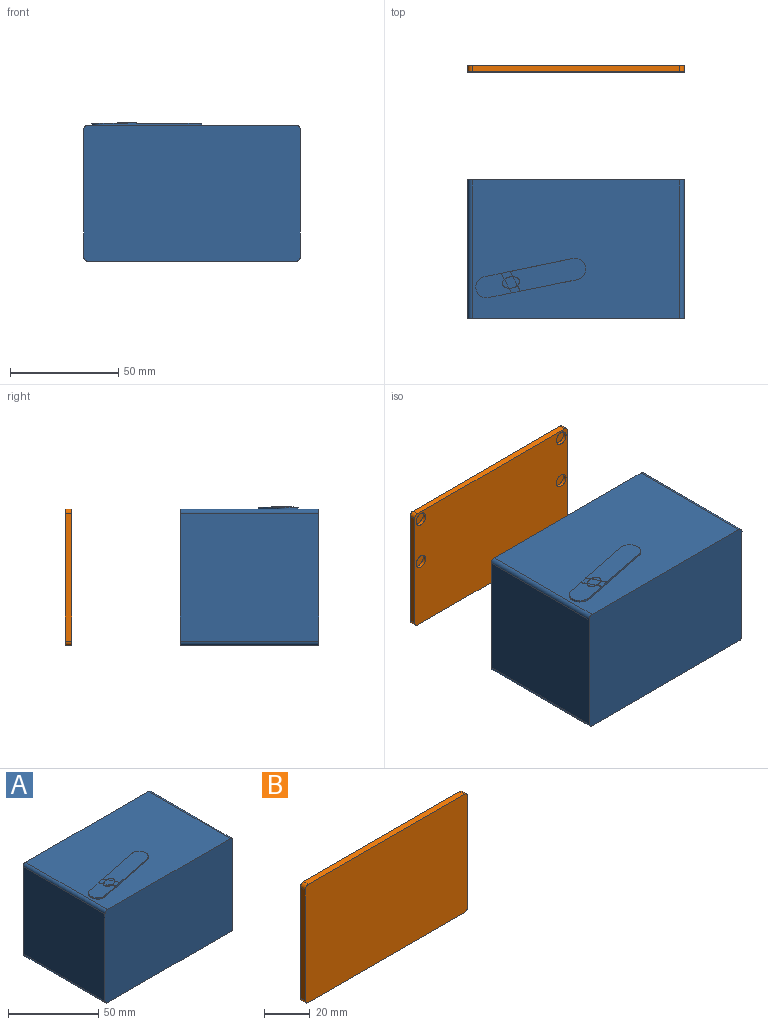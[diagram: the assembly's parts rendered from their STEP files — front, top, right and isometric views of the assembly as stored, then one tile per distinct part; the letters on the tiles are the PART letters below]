
ASSEMBLY  parts=2 mates=1
PART A: 54 faces, bbox 100x64x64.2 mm
  f0: plane 5.34x3.69mm, normal (0,0,1), area 10.9mm2, adj f42,f47,f48,f51
  f1: plane 96x64mm, normal (0,0,1), area 5652.7mm2, adj f2,f7,f39,f40,f41,f42,f43,f45
  f2: plane 100x63mm, normal (0,1,0), area 2484.3mm2, adj f1,f3,f4,f6,f8,f9,f10,f11
  f3: plane 48.15x29.5mm, normal (0,0,-1), area 1420.4mm2, adj f2,f5,f14,f18
  f4: plane 48.15x29.5mm, normal (0,0,1), area 1420.4mm2, adj f2,f5,f14,f18
  f5: cylinder r=14.35mm len=29.5mm, axis (1,0,0), area 1329.9mm2, adj f3,f4,f14,f18
  f6: plane 64x59mm, normal (-1,0,0), area 3776mm2, adj f2,f7,f37,f39
  f7: plane 100x63mm, normal (0,-1,0), area 6296.6mm2, adj f1,f6,f8,f9,f37,f38,f39,f40
  f8: plane 64x59mm, normal (1,0,0), area 3776mm2, adj f2,f7,f38,f40
  f9: plane 96x64mm, normal (0,0,-1), area 6144mm2, adj f2,f7,f37,f38
  f10: plane 62.5x28.7mm, normal (1,0,0), area 1705.4mm2, adj f2,f11,f12,f13
  f11: plane 59.5x48.15mm, normal (0,0,-1), area 2864.9mm2, adj f2,f10,f13,f16
  f12: plane 59.5x48.15mm, normal (0,0,1), area 2864.9mm2, adj f2,f10,f13,f16
  f13: cylinder r=14.35mm len=59.5mm, axis (1,0,0), area 2682.4mm2, adj f10,f11,f12,f16
  f14: plane 62.5x28.7mm, normal (-1,0,0), area 1705.4mm2, adj f2,f3,f4,f5
  f15: plane 63x7.5mm, normal (0,0,-1), area 472.5mm2, adj f2,f16,f18,f19
  f16: plane 63x30.7mm, normal (1,0,0), area 228.7mm2, adj f2,f11,f12,f13,f15,f17,f19
  f17: plane 63x7.5mm, normal (0,0,1), area 472.5mm2, adj f2,f16,f18,f19
  f18: plane 63x30.7mm, normal (-1,0,0), area 228.7mm2, adj f2,f3,f4,f5,f15,f17,f19
  f19: plane 30.7x7.5mm, normal (0,1,0), area 230.2mm2, adj f15,f16,f17,f18
  f20: plane 73x42mm, normal (0,0,1), area 2851mm2, adj f2,f21,f23,f24,f25,f27,f28
  f21: plane 42x12mm, normal (1,0,0), area 504mm2, adj f2,f20,f22,f24
  f22: plane 73x42mm, normal (0,0,-1), area 3066mm2, adj f2,f21,f23,f24
  f23: plane 42x12mm, normal (-1,0,0), area 504mm2, adj f2,f20,f22,f24
  f24: plane 73x12mm, normal (0,1,0), area 876mm2, adj f20,f21,f22,f23
  f25: plane 25x3mm, normal (-1,0,0), area 75mm2, adj f2,f20,f26,f28
  f26: plane 25x8.6mm, normal (0,0,1), area 215mm2, adj f2,f25,f27,f28
  f27: plane 25x3mm, normal (1,0,0), area 75mm2, adj f2,f20,f26,f28
  f28: plane 8.6x3mm, normal (0,1,0), area 25.8mm2, adj f20,f25,f26,f27
  f29: cylinder r=3.17mm len=6.33mm, axis (0,1,0), area 32mm2, adj f2,f30
  f30: plane 6.33x6.33mm, normal (0,1,0), area 31.5mm2, adj f29
  f31: cylinder r=3.17mm len=6.33mm, axis (0,1,0), area 32mm2, adj f2,f32
  f32: plane 6.33x6.33mm, normal (0,1,0), area 31.5mm2, adj f31
  f33: cylinder r=3.17mm len=6.33mm, axis (0,1,0), area 32mm2, adj f2,f34
  f34: plane 6.33x6.33mm, normal (0,1,0), area 31.5mm2, adj f33
  f35: cylinder r=3.17mm len=6.33mm, axis (0,1,0), area 32mm2, adj f2,f36
  f36: plane 6.33x6.33mm, normal (0,1,0), area 31.5mm2, adj f35
  f37: cylinder r=2mm len=64mm, axis (0,-1,0), area 201.1mm2, adj f2,f6,f7,f9
  f38: cylinder r=2mm len=64mm, axis (0,1,0), area 201.1mm2, adj f2,f7,f8,f9
  f39: cylinder r=2mm len=64mm, axis (0,1,0), area 201.1mm2, adj f1,f2,f6,f7
  f40: cylinder r=2mm len=64mm, axis (0,-1,0), area 201.1mm2, adj f1,f2,f7,f8
  f41: plane 39.89x8.05mm, normal (0.2,-0.98,0), area 33.4mm2, adj f1,f43,f44,f45,f46,f47,f48,f49
  f42: plane 39.83x8.24mm, normal (-0.2,0.98,0), area 33.4mm2, adj f0,f1,f43,f44,f45,f46,f47,f48
  f43: cylinder r=5mm len=10mm, axis (0,0,-1), area 14.2mm2, adj f1,f41,f42,f44
  f44: plane 16.54x11.41mm, normal (0,0,1), area 131.4mm2, adj f41,f42,f43,f47
  f45: cylinder r=5mm len=9.9mm, axis (0,0,-1), area 12.6mm2, adj f1,f41,f42,f46
  f46: plane 34.96x15.19mm, normal (0,0,1), area 318.9mm2, adj f41,f42,f45,f48
  f47: plane 9.08x4.73mm, normal (-0.89,-0.46,0), area 2mm2, adj f0,f41,f42,f44,f49,f50
  f48: plane 9.1x4.74mm, normal (0.89,0.46,0), area 2.1mm2, adj f0,f41,f42,f46,f49,f53
  f49: plane 5.2x3.45mm, normal (0,0,1), area 9.8mm2, adj f41,f47,f48,f51
  f50: plane 4.08x3.1mm, normal (0,0,-1), area 6.2mm2, adj f47,f51
  f51: extruded ~7.85x5.33mm, area 4.2mm2, adj f0,f49,f50,f52,f53
  f52: plane 7.86x5.35mm, normal (0,0,1), area 32.6mm2, adj f51
  f53: plane 4.04x3.04mm, normal (0,0,-1), area 6mm2, adj f48,f51
PART B: 18 faces, bbox 100x3x63 mm
  f0: plane 59x3mm, normal (1,0,0), area 177mm2, adj f4,f5,f14,f17
  f1: plane 96x3mm, normal (0,0,1), area 288mm2, adj f4,f5,f14,f15
  f2: plane 59x3mm, normal (-1,0,0), area 177mm2, adj f4,f5,f15,f16
  f3: plane 96x3mm, normal (0,0,-1), area 288mm2, adj f4,f5,f16,f17
  f4: plane 100x63mm, normal (0,-1,0), area 6296.6mm2, adj f0,f1,f2,f3,f14,f15,f16,f17
  f5: plane 100x63mm, normal (0,1,0), area 6170.7mm2, adj f0,f1,f2,f3,f6,f8,f10,f12
  f6: cylinder r=3.17mm len=6.33mm, axis (0,1,0), area 33.2mm2, adj f5,f7
  f7: plane 6.33x6.33mm, normal (0,1,0), area 31.5mm2, adj f6
  f8: cylinder r=3.17mm len=6.33mm, axis (0,1,0), area 33.2mm2, adj f5,f9
  f9: plane 6.33x6.33mm, normal (0,1,0), area 31.5mm2, adj f8
  f10: cylinder r=3.17mm len=6.33mm, axis (0,1,0), area 33.2mm2, adj f5,f11
  f11: plane 6.33x6.33mm, normal (0,1,0), area 31.5mm2, adj f10
  f12: cylinder r=3.17mm len=6.33mm, axis (0,1,0), area 33.2mm2, adj f5,f13
  f13: plane 6.33x6.33mm, normal (0,1,0), area 31.5mm2, adj f12
  f14: cylinder r=2mm len=3mm, axis (0,-1,0), area 9.4mm2, adj f0,f1,f4,f5
  f15: cylinder r=2mm len=3mm, axis (0,1,0), area 9.4mm2, adj f1,f2,f4,f5
  f16: cylinder r=2mm len=3mm, axis (0,-1,0), area 9.4mm2, adj f2,f3,f4,f5
  f17: cylinder r=2mm len=3mm, axis (0,1,0), area 9.4mm2, adj f0,f3,f4,f5
PLACE A rot(axis=(-0.15,0.99,0.03),0deg) t=(92.57,-108.24,-21.47)mm fixed
PLACE B rot(axis=(0,0,-1),180deg) t=(118.4,5.76,-21.47)mm
MATE slider A.f2 <-> B.f5  axis (0,1,0) through (42.57,-44.24,41.53)mm
